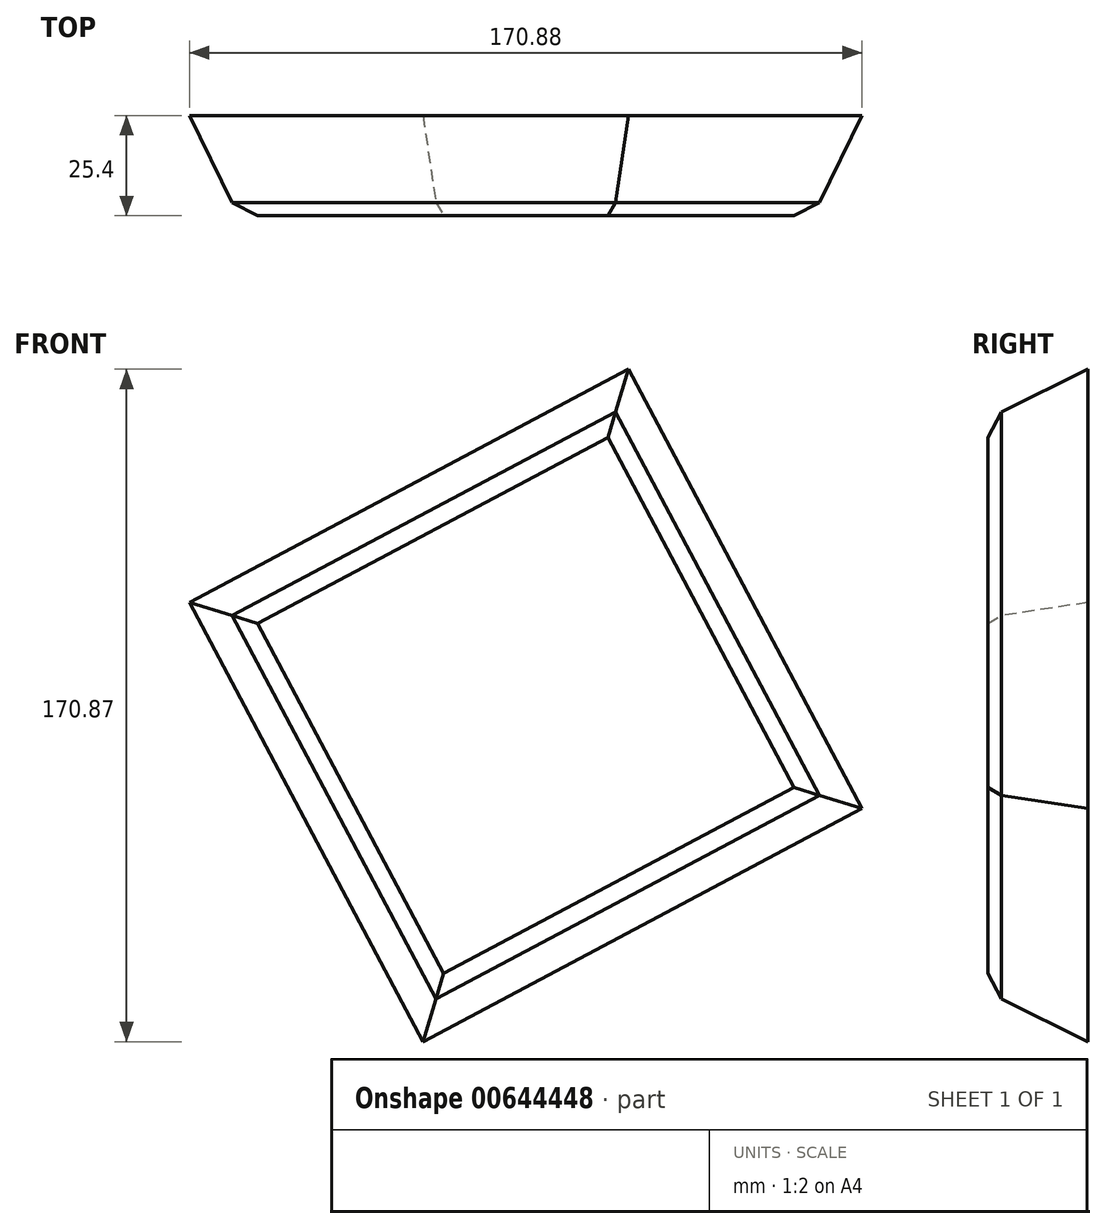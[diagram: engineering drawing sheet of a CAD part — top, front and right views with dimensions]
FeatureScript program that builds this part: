
annotation { "Feature Type Name" : "Feature", "Feature Type Description" : "" }
export const myFeature = defineFeature(function(context is Context, id is Id, definition is map)
    precondition{}
    {
        {
            var Q0;
            Q0=qCreatedBy(makeId("Front.planeOp"),FACE);
            var sketch = newSketch(context, id + "F0", { "sketchPlane" : qUnion([Q0])});
            skCircle(sketch, "E0.cCircle", {"center": v(0, 64.65) * mm, "radius": 76.27 * mm, "construction": true});
            skLineSegment(sketch, "E0.0", {"start": v(72.93, 42.34) * mm, "end": v(-22.31, -8.28) * mm});
            skLineSegment(sketch, "E0.1", {"start": v(-22.31, -8.28) * mm, "end": v(-72.93, 86.97) * mm});
            skLineSegment(sketch, "E0.2", {"start": v(-72.93, 86.97) * mm, "end": v(22.31, 137.58) * mm});
            skLineSegment(sketch, "E0.3", {"start": v(22.31, 137.58) * mm, "end": v(72.93, 42.34) * mm});
            skSolve(sketch);
        }
        {
            var Q0;
            Q0 = qSketchRegion(id + "FnEeKLTr2fGQpWH_0", true);
            var Q1;
            Q1=makeQuery(id+"F0.imprint","IMPRINT",FACE,{"disambiguationData":[TD([[makeQuery(id+"F0.imprint","IMPRINT",EDGE,{"derivedFrom":sQuery(id+"F0.wireOp",EDGE,"E0.0")}),-1.0]])]});
            extrude(context, id + "F1", {"entities" : qUnion([Q0, Q1]), "oppositeDirection" : true, "depth" : 25.4 * mm, "offsetDistance" : 25.4 * mm, "hasDraft" : true, "draftAngle" : 20 * degree});
        }
        {
            var Q0;
            Q0=makeQuery(id+"F1.opExtrude","CAP_FACE",FACE,{"disambiguationData":[OSD([sQuery(id+"F0.wireOp",EDGE,"E0.0"),sQuery(id+"F0.wireOp",EDGE,"E0.1"),sQuery(id+"F0.wireOp",EDGE,"E0.2"),sQuery(id+"F0.wireOp",EDGE,"E0.3")])],"isStart":true});
            chamfer(context, id + "F2", {"entities" : qUnion([Q0]), "width" : 5.08 * mm, "tangentPropagation" : true});
        }
    });
